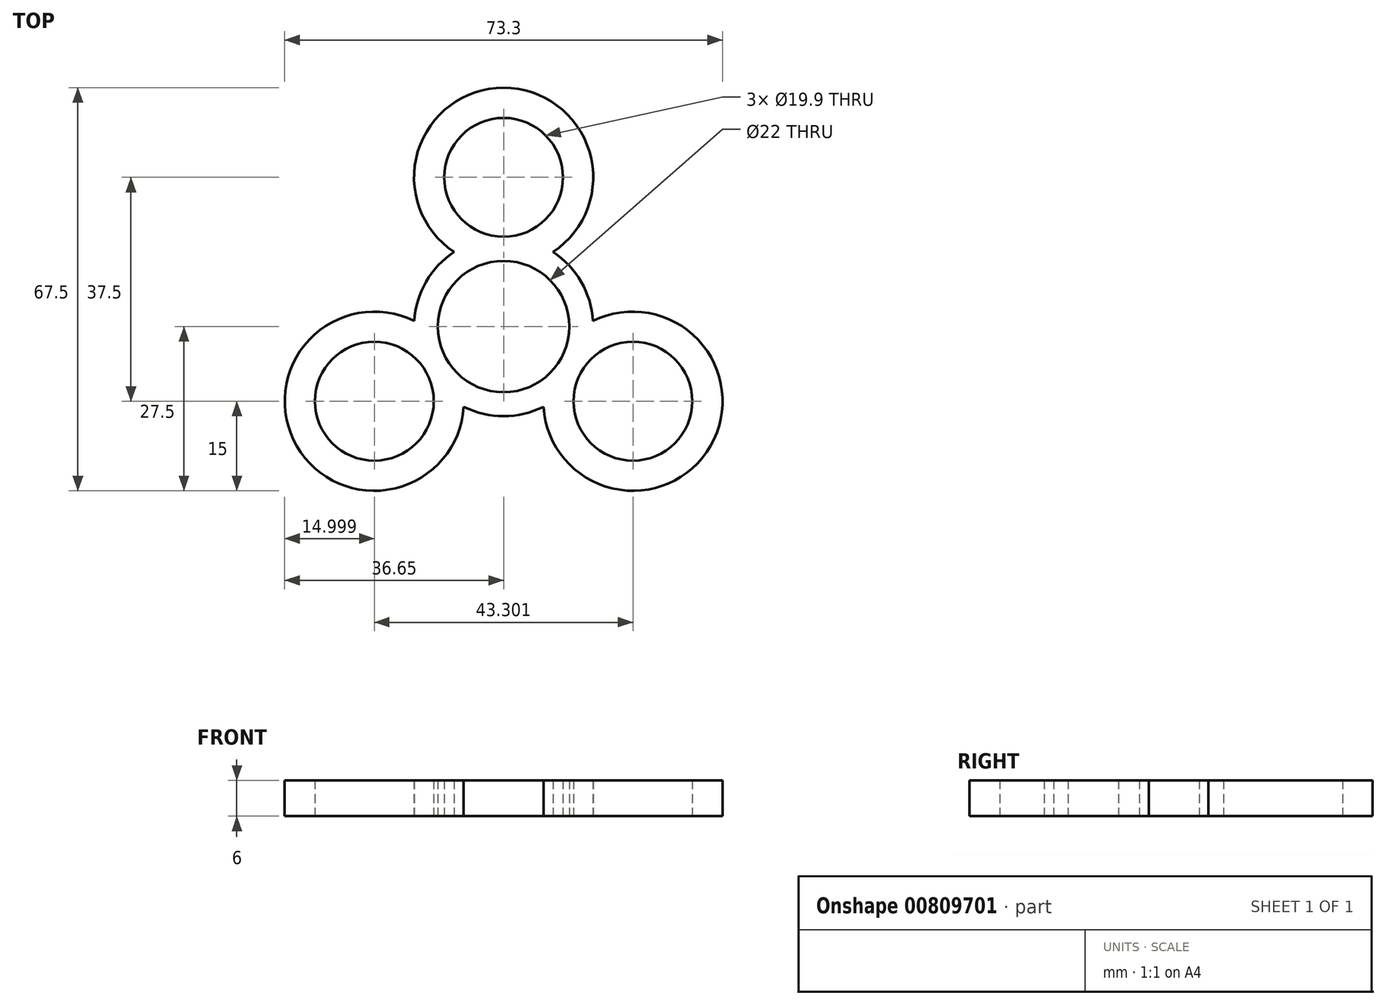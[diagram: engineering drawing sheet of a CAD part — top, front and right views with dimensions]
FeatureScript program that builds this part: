
annotation { "Feature Type Name" : "Feature", "Feature Type Description" : "" }
export const myFeature = defineFeature(function(context is Context, id is Id, definition is map)
    precondition{}
    {
        {
            var Q0;
            Q0=qCreatedBy(makeId("Top.planeOp"),FACE);
            var sketch = newSketch(context, id + "F0", { "sketchPlane" : qUnion([Q0])});
            skCircle(sketch, "E0", {"center": v(0, 25) * mm, "radius": 9.95 * mm});
            skArc(sketch, "E1", {"start": v(8.3, 12.5) * mm, "mid": v(0, 40) * mm, "end": v(-8.3, 12.5) * mm});
            skArc(sketch, "E2", {"start": v(9.53, 5.5) * mm, "mid": v(0, 11) * mm, "end": v(-9.53, 5.5) * mm});
            skArc(sketch, "E3", {"start": v(-8.3, 12.5) * mm, "mid": v(-10.93, 10.27) * mm, "end": v(-13, 7.5) * mm});
            skArc(sketch, "E4.trimOffspring", {"start": v(13, 7.5) * mm, "mid": v(10.93, 10.27) * mm, "end": v(8.3, 12.5) * mm});
            skArc(sketch, "E5.1.0", {"start": v(-9.53, 5.5) * mm, "mid": v(-9.53, -5.5) * mm, "end": v(0, -11) * mm});
            skArc(sketch, "E5.1.1", {"start": v(-13, 7.5) * mm, "mid": v(-14.36, 4.33) * mm, "end": v(-14.97, 0.93) * mm});
            skArc(sketch, "E5.1.2", {"start": v(-6.68, -13.43) * mm, "mid": v(-3.43, -14.6) * mm, "end": v(0, -15) * mm});
            skArc(sketch, "E5.1.3", {"start": v(-14.97, 0.93) * mm, "mid": v(-34.64, -20) * mm, "end": v(-6.68, -13.43) * mm});
            skCircle(sketch, "E5.1.4", {"center": v(-21.65, -12.5) * mm, "radius": 9.95 * mm});
            skArc(sketch, "E5.2.0", {"start": v(0, -11) * mm, "mid": v(9.53, -5.5) * mm, "end": v(9.53, 5.5) * mm});
            skArc(sketch, "E5.2.1", {"start": v(0, -15) * mm, "mid": v(3.43, -14.6) * mm, "end": v(6.68, -13.43) * mm});
            skArc(sketch, "E5.2.2", {"start": v(14.97, 0.93) * mm, "mid": v(14.36, 4.33) * mm, "end": v(13, 7.5) * mm});
            skArc(sketch, "E5.2.3", {"start": v(6.68, -13.43) * mm, "mid": v(34.64, -20) * mm, "end": v(14.97, 0.93) * mm});
            skCircle(sketch, "E5.2.4", {"center": v(21.65, -12.5) * mm, "radius": 9.95 * mm});
            skSolve(sketch);
        }
        {
            var Q0;
            Q0 = qSketchRegion(id + "F0", true);
            extrude(context, id + "F1", {"entities" : qUnion([Q0]), "depth" : 6 * mm, "offsetDistance" : 25 * mm});
        }
    });
